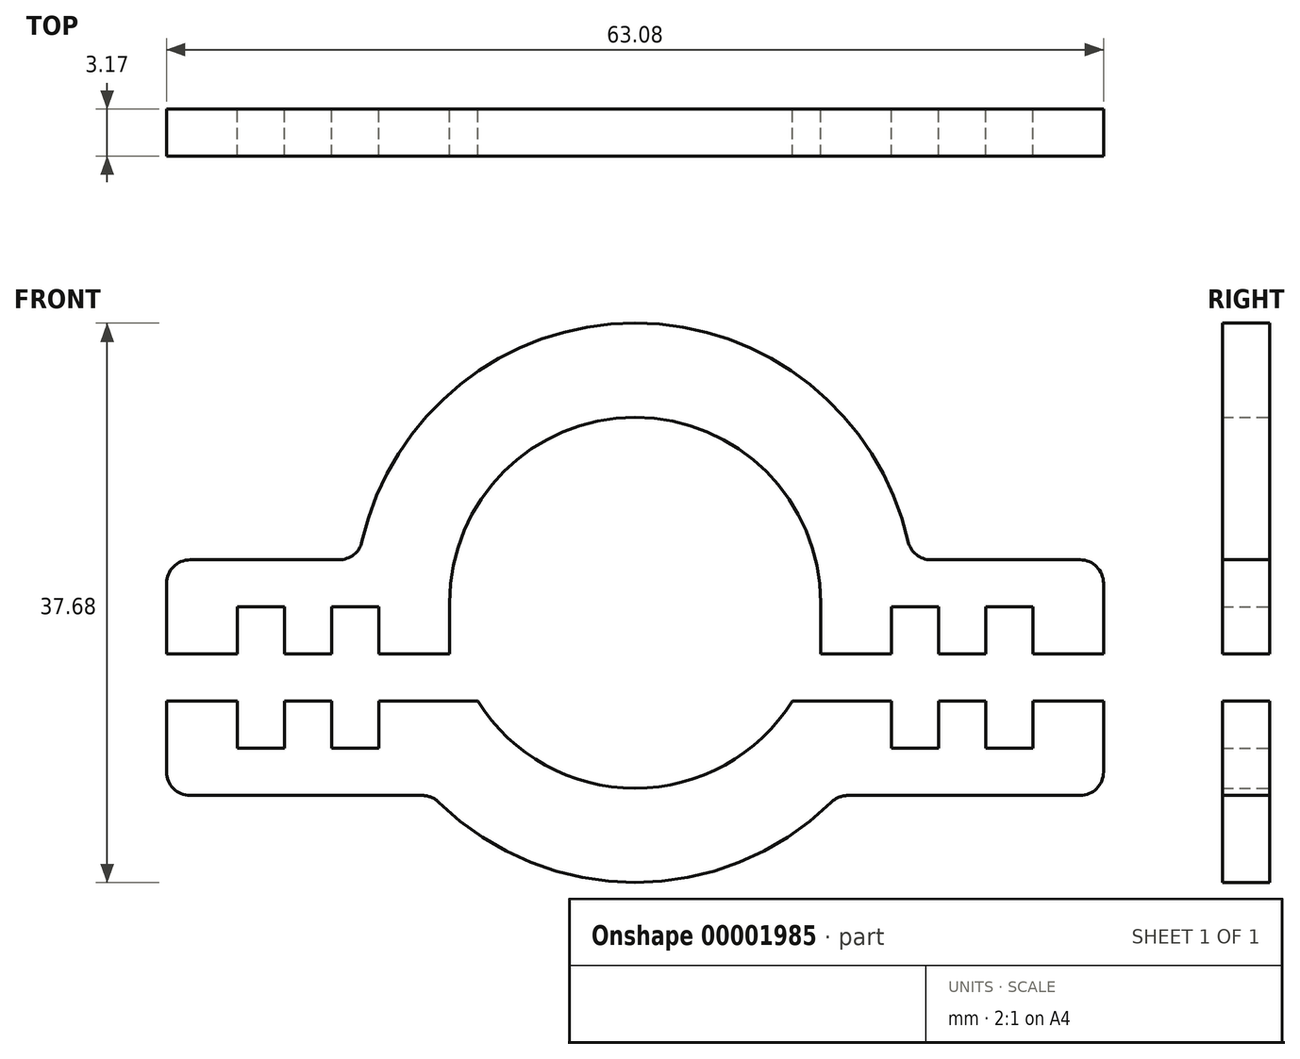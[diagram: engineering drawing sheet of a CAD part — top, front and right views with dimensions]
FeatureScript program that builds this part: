
annotation { "Feature Type Name" : "Feature", "Feature Type Description" : "" }
export const myFeature = defineFeature(function(context is Context, id is Id, definition is map)
    precondition{}
    {
        {
            var Q0;
            Q0=qCreatedBy(makeId("Front.planeOp"),FACE);
            var sketch = newSketch(context, id + "F0", { "sketchPlane" : qUnion([Q0])});
            skArc(sketch, "E0", {"start": v(0, 12.5) * mm, "mid": v(-8.83, 8.83) * mm, "end": v(-12.5, 0) * mm});
            skLineSegment(sketch, "E1", {"start": v(-12.5, -3.45) * mm, "end": v(-17.25, -3.45) * mm});
            skLineSegment(sketch, "E2", {"start": v(-31.54, -3.45) * mm, "end": v(-31.54, 1.3) * mm});
            skLineSegment(sketch, "E3", {"start": v(-29.95, 2.9) * mm, "end": v(-19.93, 2.9) * mm});
            skArc(sketch, "E4", {"start": v(0, 18.84) * mm, "mid": v(-11.77, 14.71) * mm, "end": v(-18.38, 4.13) * mm});
            skPoint(sketch, "E5", {"position": v(0, 18.84) * mm});
            skPoint(sketch, "E6.visualSharp", {"position": v(-31.54, 2.9) * mm});
            skArc(sketch, "E6.filletArc", {"start": v(-29.95, 2.9) * mm, "mid": v(-31.08, 2.43) * mm, "end": v(-31.54, 1.3) * mm});
            skPoint(sketch, "E7.visualSharp", {"position": v(-18.62, 2.9) * mm});
            skArc(sketch, "E7.filletArc", {"start": v(-19.93, 2.9) * mm, "mid": v(-18.94, 3.24) * mm, "end": v(-18.38, 4.13) * mm});
            skArc(sketch, "E8", {"start": v(0, 3.45) * mm, "mid": v(-3.45, 0) * mm, "end": v(0, -3.45) * mm, "construction": true});
            skLineSegment(sketch, "E9", {"start": v(-12.5, 0) * mm, "end": v(-12.5, -3.45) * mm});
            skPoint(sketch, "E10", {"position": v(-22.02, -3.45) * mm});
            skLineSegment(sketch, "E11.rect.bottom", {"start": v(-20.43, -3.45) * mm, "end": v(-23.6, -3.45) * mm});
            skLineSegment(sketch, "E11.rect.left", {"start": v(-20.43, -3.45) * mm, "end": v(-20.43, -0.28) * mm});
            skLineSegment(sketch, "E11.rect.right", {"start": v(-23.6, -3.45) * mm, "end": v(-23.6, -0.28) * mm});
            skPoint(sketch, "E11.rect.middle", {"position": v(-22.02, -1.87) * mm});
            skLineSegment(sketch, "E12", {"start": v(-23.6, -0.28) * mm, "end": v(-26.78, -0.28) * mm});
            skLineSegment(sketch, "E13", {"start": v(-26.78, -0.28) * mm, "end": v(-26.78, -3.45) * mm});
            skLineSegment(sketch, "E14", {"start": v(-20.43, -0.28) * mm, "end": v(-17.25, -0.28) * mm});
            skLineSegment(sketch, "E15", {"start": v(-17.25, -0.28) * mm, "end": v(-17.25, -3.45) * mm});
            skLineSegment(sketch, "E16.trimOffspring", {"start": v(-26.78, -3.45) * mm, "end": v(-31.54, -3.45) * mm});
            skArc(sketch, "E17", {"start": v(-10.59, -6.63) * mm, "mid": v(-6.05, -10.93) * mm, "end": v(0, -12.5) * mm});
            skPoint(sketch, "E18", {"position": v(0, 12.5) * mm});
            skPoint(sketch, "E19", {"position": v(0, -12.5) * mm});
            skLineSegment(sketch, "E20", {"start": v(-10.59, -6.63) * mm, "end": v(-17.25, -6.63) * mm});
            skLineSegment(sketch, "E21", {"start": v(-31.54, -6.63) * mm, "end": v(-31.54, -11.4) * mm});
            skArc(sketch, "E22", {"start": v(-13.2, -13.43) * mm, "mid": v(-7.14, -17.44) * mm, "end": v(0, -18.84) * mm});
            skLineSegment(sketch, "E23", {"start": v(-29.95, -12.98) * mm, "end": v(-14.32, -12.98) * mm});
            skLineSegment(sketch, "E24", {"start": v(-26.78, -6.63) * mm, "end": v(-26.78, -9.8) * mm});
            skLineSegment(sketch, "E25", {"start": v(-26.78, -9.8) * mm, "end": v(-23.6, -9.8) * mm});
            skLineSegment(sketch, "E26", {"start": v(-23.6, -9.8) * mm, "end": v(-23.6, -6.63) * mm});
            skLineSegment(sketch, "E27", {"start": v(-20.43, -6.63) * mm, "end": v(-20.43, -9.8) * mm});
            skLineSegment(sketch, "E28", {"start": v(-20.43, -9.8) * mm, "end": v(-17.25, -9.8) * mm});
            skLineSegment(sketch, "E29", {"start": v(-17.25, -9.8) * mm, "end": v(-17.25, -6.63) * mm});
            skLineSegment(sketch, "E30.trimOffspring", {"start": v(-26.78, -6.63) * mm, "end": v(-31.54, -6.63) * mm});
            skLineSegment(sketch, "E31.trimOffspring", {"start": v(-20.43, -6.63) * mm, "end": v(-23.6, -6.63) * mm});
            skPoint(sketch, "E32.visualSharp", {"position": v(-31.54, -12.98) * mm});
            skArc(sketch, "E32.filletArc", {"start": v(-31.54, -11.4) * mm, "mid": v(-31.08, -12.51) * mm, "end": v(-29.95, -12.98) * mm});
            skPoint(sketch, "E33.visualSharp", {"position": v(-13.66, -12.98) * mm});
            skArc(sketch, "E33.filletArc", {"start": v(-13.2, -13.43) * mm, "mid": v(-13.72, -13.1) * mm, "end": v(-14.32, -12.98) * mm});
            skPoint(sketch, "E34", {"position": v(0, 3.45) * mm});
            skPoint(sketch, "E35", {"position": v(0, -3.45) * mm});
            skLineSegment(sketch, "E36.0.MirrorCS", {"start": v(20.43, -3.45) * mm, "end": v(23.6, -3.45) * mm});
            skArc(sketch, "E36.1.MirrorCS", {"start": v(13.2, -13.43) * mm, "mid": v(13.72, -13.1) * mm, "end": v(14.32, -12.98) * mm});
            skArc(sketch, "E36.2.MirrorCS", {"start": v(29.95, 2.9) * mm, "mid": v(31.08, 2.43) * mm, "end": v(31.54, 1.3) * mm});
            skArc(sketch, "E36.3.MirrorCS", {"start": v(19.93, 2.9) * mm, "mid": v(18.94, 3.24) * mm, "end": v(18.38, 4.13) * mm});
            skArc(sketch, "E36.4.MirrorCS", {"start": v(31.54, -11.4) * mm, "mid": v(31.08, -12.51) * mm, "end": v(29.95, -12.98) * mm});
            skLineSegment(sketch, "E36.5.MirrorCS", {"start": v(20.43, -3.45) * mm, "end": v(23.6, -3.45) * mm});
            skArc(sketch, "E36.6.MirrorCS", {"start": v(13.2, -13.43) * mm, "mid": v(7.14, -17.44) * mm, "end": v(0, -18.84) * mm});
            skLineSegment(sketch, "E36.7.MirrorCS", {"start": v(10.59, -6.63) * mm, "end": v(17.25, -6.63) * mm});
            skLineSegment(sketch, "E36.8.MirrorCS", {"start": v(12.5, 0) * mm, "end": v(12.5, -3.45) * mm});
            skPoint(sketch, "E36.9.MirrorP", {"position": v(22.02, -3.45) * mm});
            skLineSegment(sketch, "E36.10.MirrorCS", {"start": v(26.78, -3.45) * mm, "end": v(31.54, -3.45) * mm});
            skLineSegment(sketch, "E36.13.MirrorCS", {"start": v(17.25, -0.28) * mm, "end": v(17.25, -3.45) * mm});
            skLineSegment(sketch, "E36.14.MirrorCS", {"start": v(31.54, -3.45) * mm, "end": v(31.54, 1.3) * mm});
            skLineSegment(sketch, "E36.15.MirrorCS", {"start": v(20.43, -0.28) * mm, "end": v(17.25, -0.28) * mm});
            skPoint(sketch, "E36.16.MirrorP", {"position": v(31.54, 2.9) * mm});
            skLineSegment(sketch, "E36.17.MirrorCS", {"start": v(12.5, -3.45) * mm, "end": v(17.25, -3.45) * mm});
            skLineSegment(sketch, "E36.18.MirrorCS", {"start": v(26.78, -9.8) * mm, "end": v(23.6, -9.8) * mm});
            skArc(sketch, "E36.20.MirrorCS", {"start": v(0, 18.84) * mm, "mid": v(11.77, 14.71) * mm, "end": v(18.38, 4.13) * mm});
            skLineSegment(sketch, "E36.21.MirrorCS", {"start": v(29.95, -12.98) * mm, "end": v(14.32, -12.98) * mm});
            skPoint(sketch, "E36.22.MirrorP", {"position": v(13.66, -12.98) * mm});
            skLineSegment(sketch, "E36.23.MirrorCS", {"start": v(26.78, -6.63) * mm, "end": v(26.78, -9.8) * mm});
            skLineSegment(sketch, "E36.24.MirrorCS", {"start": v(23.6, -9.8) * mm, "end": v(23.6, -6.63) * mm});
            skPoint(sketch, "E36.25.MirrorP", {"position": v(18.62, 2.9) * mm});
            skArc(sketch, "E36.26.MirrorCS", {"start": v(0, 3.45) * mm, "mid": v(3.45, 0) * mm, "end": v(0, -3.45) * mm, "construction": true});
            skPoint(sketch, "E36.28.MirrorP", {"position": v(31.54, -12.98) * mm});
            skLineSegment(sketch, "E36.29.MirrorCS", {"start": v(23.6, -3.45) * mm, "end": v(23.6, -0.28) * mm});
            skLineSegment(sketch, "E36.30.MirrorCS", {"start": v(20.43, -3.45) * mm, "end": v(20.43, -0.28) * mm});
            skLineSegment(sketch, "E36.31.MirrorCS", {"start": v(29.95, 2.9) * mm, "end": v(19.93, 2.9) * mm});
            skLineSegment(sketch, "E36.32.MirrorCS", {"start": v(20.43, -9.8) * mm, "end": v(17.25, -9.8) * mm});
            skLineSegment(sketch, "E36.33.MirrorCS", {"start": v(26.78, -0.28) * mm, "end": v(26.78, -3.45) * mm});
            skLineSegment(sketch, "E36.34.MirrorCS", {"start": v(23.6, -0.28) * mm, "end": v(26.78, -0.28) * mm});
            skArc(sketch, "E36.35.MirrorCS", {"start": v(10.59, -6.63) * mm, "mid": v(6.05, -10.93) * mm, "end": v(0, -12.5) * mm});
            skLineSegment(sketch, "E36.36.MirrorCS", {"start": v(20.43, -6.63) * mm, "end": v(23.6, -6.63) * mm});
            skLineSegment(sketch, "E36.37.MirrorCS", {"start": v(31.54, -6.63) * mm, "end": v(31.54, -11.4) * mm});
            skLineSegment(sketch, "E36.38.MirrorCS", {"start": v(26.78, -6.63) * mm, "end": v(31.54, -6.63) * mm});
            skLineSegment(sketch, "E36.39.MirrorCS", {"start": v(17.25, -9.8) * mm, "end": v(17.25, -6.63) * mm});
            skLineSegment(sketch, "E36.40.MirrorCS", {"start": v(20.43, -6.63) * mm, "end": v(20.43, -9.8) * mm});
            skArc(sketch, "E36.41.MirrorCS", {"start": v(0, 12.5) * mm, "mid": v(8.83, 8.83) * mm, "end": v(12.5, 0) * mm});
            skPoint(sketch, "E36.42.MirrorP", {"position": v(22.02, -1.87) * mm});
            skSolve(sketch);
        }
        {
            var Q0;
            Q0=makeQuery(id+"F0.imprint","IMPRINT",FACE,{"disambiguationData":[TD([[makeQuery(id+"F0.imprint","IMPRINT",EDGE,{"derivedFrom":sQuery(id+"F0.wireOp",EDGE,"E0")}),-1.0]])]});
            var Q1;
            Q1=makeQuery(id+"F0.imprint","IMPRINT",FACE,{"disambiguationData":[TD([[makeQuery(id+"F0.imprint","IMPRINT",EDGE,{"derivedFrom":sQuery(id+"F0.wireOp",EDGE,"E17")}),-1.0]])]});
            extrude(context, id + "F1", {"entities" : qUnion([Q0, Q1]), "depth" : 3.17 * mm});
        }
    });
